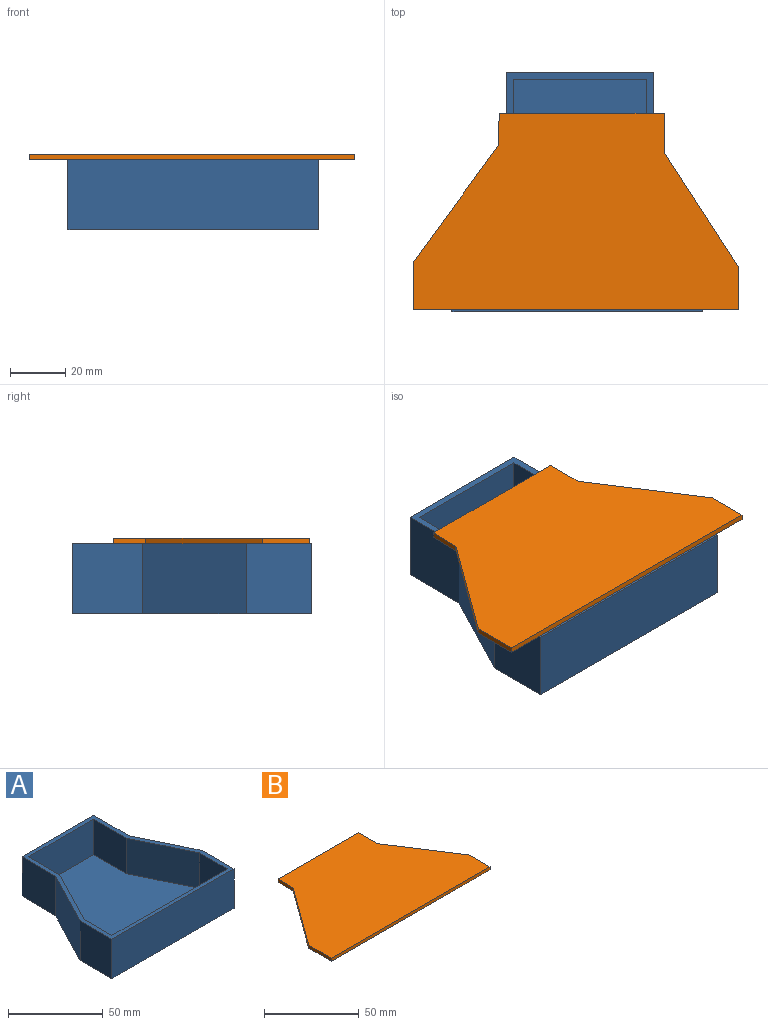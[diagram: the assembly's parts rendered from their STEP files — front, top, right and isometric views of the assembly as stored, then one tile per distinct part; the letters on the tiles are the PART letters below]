
ASSEMBLY  parts=2 mates=1
PART A: 19 faces, bbox 90.9x86.9x25.4 mm
  f0: plane 90.85x86.86mm, normal (0,0,1), area 804mm2, adj f1,f2,f3,f4,f5,f6,f7,f8
  f1: plane 25.45x25.4mm, normal (-1,0.01,0), area 646.5mm2, adj f0,f2,f8,f9
  f2: plane 37.63x25.4mm, normal (-0.89,0.46,0), area 1076.8mm2, adj f0,f1,f3,f9
  f3: plane 25.4x23.78mm, normal (-1,0,0), area 604mm2, adj f0,f2,f4,f9
  f4: plane 90.85x25.4mm, normal (0,-1,0), area 2307.6mm2, adj f0,f3,f5,f9
  f5: plane 25.4x23.78mm, normal (1,0,0), area 604mm2, adj f0,f4,f6,f9
  f6: plane 36.55x25.4mm, normal (0.9,0.44,0), area 1031.4mm2, adj f0,f5,f7,f9
  f7: plane 26.53x25.4mm, normal (1,0,0), area 673.9mm2, adj f0,f6,f8,f9
  f8: plane 53.29x25.4mm, normal (0,1,0), area 1353.7mm2, adj f0,f1,f7,f9
  f9: plane 90.85x86.86mm, normal (0,0,-1), area 6229.3mm2, adj f1,f2,f3,f4,f5,f6,f7,f8
  f10: plane 23.55x22.86mm, normal (1,-0.01,0), area 538.3mm2, adj f0,f11,f17,f18
  f11: plane 37.61x22.86mm, normal (0.89,-0.46,0), area 968.7mm2, adj f0,f10,f12,f18
  f12: plane 22.86x20.62mm, normal (1,0,0), area 471.4mm2, adj f0,f11,f13,f18
  f13: plane 85.77x22.86mm, normal (0,1,0), area 1960.7mm2, adj f0,f12,f14,f18
  f14: plane 22.86x20.66mm, normal (-1,0,0), area 472.2mm2, adj f0,f13,f15,f18
  f15: plane 36.55x22.86mm, normal (-0.9,-0.44,0), area 928.2mm2, adj f0,f14,f16,f18
  f16: plane 24.58x22.86mm, normal (-1,0,0), area 561.8mm2, adj f0,f15,f17,f18
  f17: plane 48.25x22.86mm, normal (0,-1,0), area 1102.9mm2, adj f0,f10,f16,f18
  f18: plane 85.77x81.78mm, normal (0,0,1), area 5425.3mm2, adj f10,f11,f12,f13,f14,f15,f16,f17
PART B: 10 faces, bbox 118x71.1x2 mm
  f0: plane 11.75x2mm, normal (-1,0.03,0), area 23.5mm2, adj f1,f7,f8,f9
  f1: plane 42.29x30.82mm, normal (-0.81,0.59,0), area 104.7mm2, adj f0,f2,f8,f9
  f2: plane 17.1x2mm, normal (-1,0,0), area 34.2mm2, adj f1,f3,f8,f9
  f3: plane 118.03x2mm, normal (0,-1,0), area 236.1mm2, adj f2,f4,f8,f9
  f4: plane 15.22x2mm, normal (1,0,0), area 30.4mm2, adj f3,f5,f8,f9
  f5: plane 41.72x27.06mm, normal (0.84,0.54,0), area 99.5mm2, adj f4,f6,f8,f9
  f6: plane 14.19x2mm, normal (1,0,0), area 28.4mm2, adj f5,f7,f8,f9
  f7: plane 59.77x2mm, normal (0,1,0), area 119.5mm2, adj f0,f6,f8,f9
  f8: plane 118.03x71.14mm, normal (0,0,1), area 6431.8mm2, adj f0,f1,f2,f3,f4,f5,f6,f7
  f9: plane 118.03x71.14mm, normal (0,0,-1), area 6431.8mm2, adj f0,f1,f2,f3,f4,f5,f6,f7
PLACE A t=(-108.47,-5.48,30.64)mm fixed
PLACE B t=(-108.46,-20.41,56.04)mm
MATE planar A.f0 <-> B.f9  axis (0,0,1) through (-106.04,-53.94,56.04)mm
